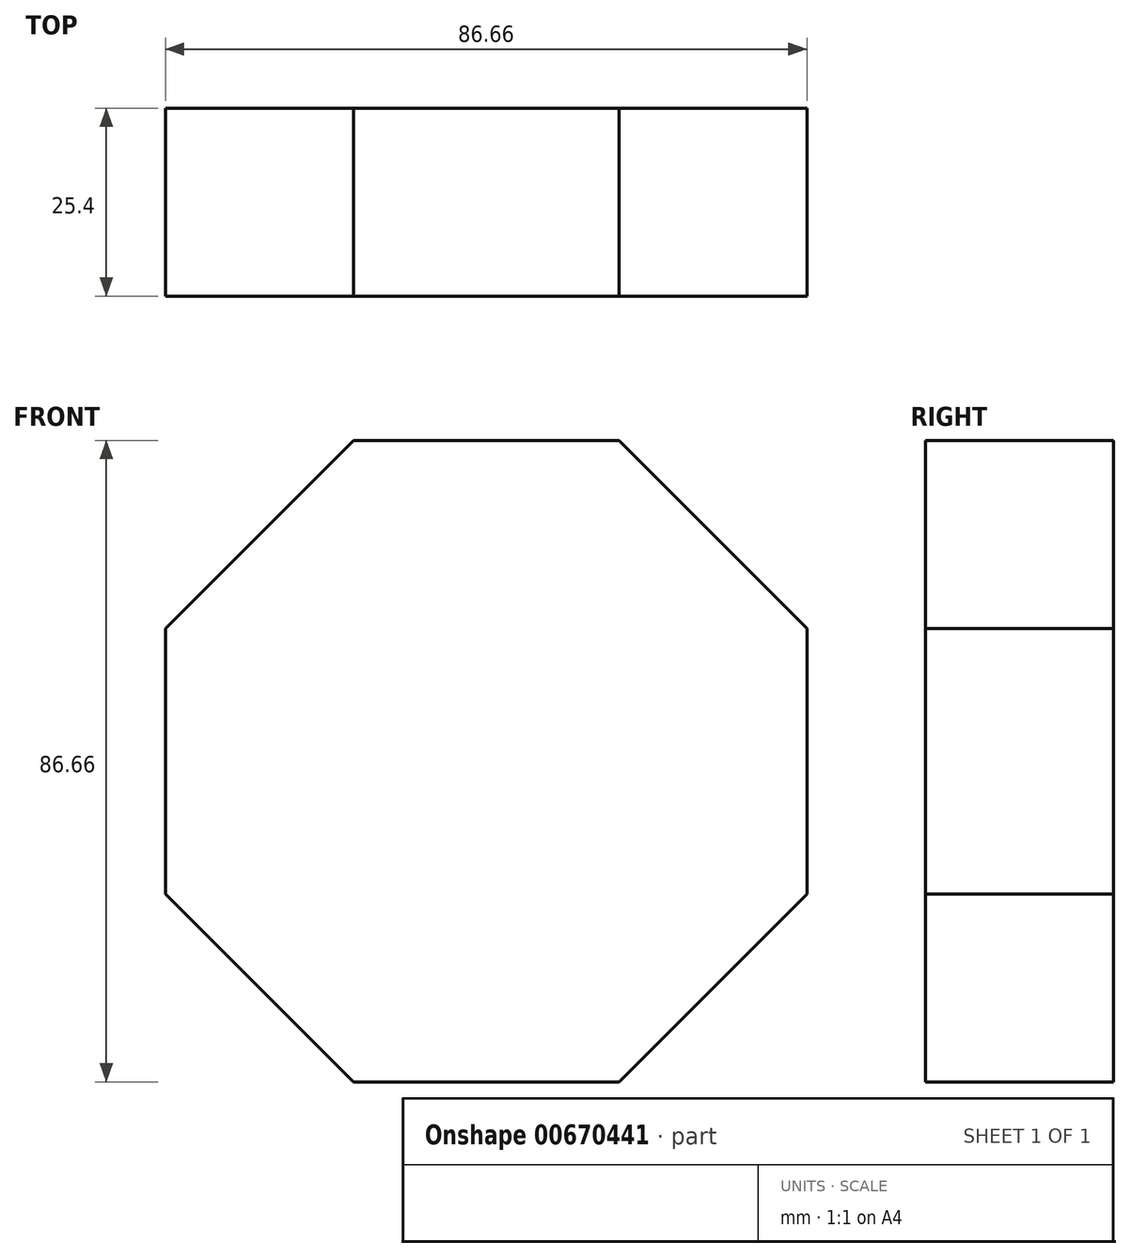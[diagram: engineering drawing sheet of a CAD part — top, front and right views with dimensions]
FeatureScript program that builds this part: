
annotation { "Feature Type Name" : "Feature", "Feature Type Description" : "" }
export const myFeature = defineFeature(function(context is Context, id is Id, definition is map)
    precondition{}
    {
        {
            var Q0;
            Q0=qCreatedBy(makeId("Front.planeOp"),FACE);
            var sketch = newSketch(context, id + "F0", { "sketchPlane" : qUnion([Q0])});
            skCircle(sketch, "E0.cCircle", {"center": v(-16.54, 26.8) * mm, "radius": 43.33 * mm, "construction": true});
            skLineSegment(sketch, "E0.0", {"start": v(1.4, -16.54) * mm, "end": v(-34.49, -16.54) * mm});
            skLineSegment(sketch, "E0.1", {"start": v(-34.49, -16.54) * mm, "end": v(-59.87, 8.84) * mm});
            skLineSegment(sketch, "E0.2", {"start": v(-59.87, 8.84) * mm, "end": v(-59.87, 44.74) * mm});
            skLineSegment(sketch, "E0.3", {"start": v(-59.87, 44.74) * mm, "end": v(-34.49, 70.12) * mm});
            skLineSegment(sketch, "E0.4", {"start": v(-34.49, 70.12) * mm, "end": v(1.4, 70.12) * mm});
            skLineSegment(sketch, "E0.5", {"start": v(1.4, 70.12) * mm, "end": v(26.8, 44.74) * mm});
            skLineSegment(sketch, "E0.6", {"start": v(26.8, 44.74) * mm, "end": v(26.8, 8.84) * mm});
            skLineSegment(sketch, "E0.7", {"start": v(26.8, 8.84) * mm, "end": v(1.4, -16.54) * mm});
            skPoint(sketch, "E0.0.midPoint", {"position": v(-16.54, -16.54) * mm});
            skSolve(sketch);
        }
        {
            var Q0;
            Q0 = qSketchRegion(id + "F0", true);
            extrude(context, id + "F1", {"entities" : qUnion([Q0]), "depth" : 25.4 * mm, "offsetDistance" : 25.4 * mm});
        }
    });
